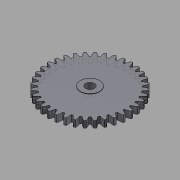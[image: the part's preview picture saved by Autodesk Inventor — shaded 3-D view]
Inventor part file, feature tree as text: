
AUTODESK INVENTOR PART (.ipt)
format: ipt  version: 2015 (Build 190159000, 159)  size: 327,168 bytes
history: native  units: in
note: dims shown in document units (in); Inventor stores cm internally (conversion verified against a paired STEP export)
features: other x13, sketch x4, plane x2
ambient origin geometry x8: Origin, YZ Plane, XZ Plane, XY Plane, X Axis, Y Axis, Z Axis, Center Point
bodies: Solid1 (feature_tree)
feature tree (19):
  other  "Spur Gear27_MIR4.ipt"
  other  "Solid1::Spur Gear27_MIR4.ipt"
  other  "TaggingFeature1"
  sketch  "Sketch1"  dims[d0=0.3937in]
  sketch  "Sketch2"  dims[d16=0.4528in d17=0.0in d41=0.0in d43=0.4528in d46=0.4528in d47=0.0in d48=0.0in]
  sketch  "Sketch3"
  sketch  "Sketch4"
  plane  "XZ Plane_1"
  plane  "Work Plane2"
  other  "Z Axis_1"
  other  "Srf1"
  other  "Srf1::Derived"
  other  "Distance iMate"
  other  "Align iMate"
  other  "Mesh iMate"
  other  "Axis iMate"
  other  "Position iMate"
  other  "Mesh iMate2"
  other  "Start plane iMate"
